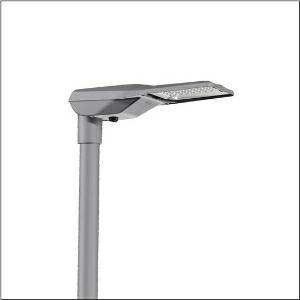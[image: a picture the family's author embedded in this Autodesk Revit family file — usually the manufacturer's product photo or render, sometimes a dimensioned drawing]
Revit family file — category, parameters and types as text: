
# Revit family: streetlight_sl_21_mini___st1_0a_5xe2d33r08gb_66de
name_source: partatom
category: Lighting Fixtures
units: mm (PartAtom-declared; Revit-internal decimal feet)

## family parameters
Cut with Voids When Loaded = No
Host = Face
Light Source = No
Part Type = Normal
Room Calculation Point = No
Round Connector Dimension = Use Diameter
Shared = No

## types (1)
- --- (1 x LED, 5940 lm, 40.4 W, 3000K)
    Apparent Load = 40 VA
    CIE Flux Codes = 37 72 97 100 100
    Color Rendering = 70
    Color Temperature = 3000K
    Default Elevation = 1800 mm
    Description = Streetlight SL 21 mini, mast luminaire, primary light control with lens, of PMMA, primary optical cover: cover, of toughened safety glass, transparent, light distribution: ST1.0a, light emission: direct distribution, primary light characteristic: asymmetric, installation type: side-entry, post-top, LED, High Power LED, rated luminous flux: 5.940lm, luminous efficacy: 147lm/W, light colour: 730, colour temperature: 3000K, control gear: ECG Smart Interface, control: flexible luminous flux parameterisation, time-dependent luminous flux control, constant luminous flux control, overheat protection, mains connection: 220..240V, AC, 50/60Hz, start of lifetime: 40W, end of lifetime: 41W, reduction: 19W, luminaire housing, of diecast aluminium, powder-coated, Siteco® metallic grey (DB 702S), corrosivity category C5 according to DIN EN ISO 12944, length: 628mm, width: 235mm, height: 110mm, spigot size: 60/76mm (post-top) and 42/60/76mm (side-entry), mast flange for spigot size: 42mm: 5XC10008XM4, 60mm: 5XC10008XM2, 76/60mm: 5XC10108XM1, protection rating (complete): IP66, insulation class (complete): insulation class II (safety insulation), certification: CE, ENEC, VDE, impact resistance: IK09, permissible operating ambient temperature for outdoor applications: -40..+50°C, standard-compliant lighting for roads and squares, packaging unit: 1 piece

Light Distribution: ST1.0a
    Height = 110 mm
    Lamp = 1 x LED
    Lamp Light Flux = 5940 lm
    Lamp Power = 40.4 W
    Lamp count = 1
    Length = 625 mm
    Luminous efficacy = 147 lm/W
    Manufacturer = Siteco
    ModVariant = No
    Model = 5XE2D33R08GB
    Number of Poles = 1
    OnlyDefault = Yes
    Power Factor = 1
    Product Name = Streetlight SL 21 mini | ST1.0a
    Product group = mast luminaire | pylon top
    ProductGroupID = 6100
    Protection Class = Protection class II
    Protection Degree = IP 66
    RLX_Detail_Level = 1
    RlxData = <blob elided: 92217 chars, md5=338c996d>
    Socket = socket
    Standby Power = 0 W
    System Light Flux = 5940 lm
    System Power = 40 W
    Type Comments = factory setting: luminous flux: 100 % | dim-lin: 254 | 812 mA
    Type Image = l_1003516.jpg
    URL = http://relux.com
    VarID = @adj_107073
    Voltage = 0 V
    Weight = 0.00 kg
    Width = 234 mm

## geometry (parser evidence)
native form markers: Blend x4, Sweep x11
no freeform markers — native parametric forms only
